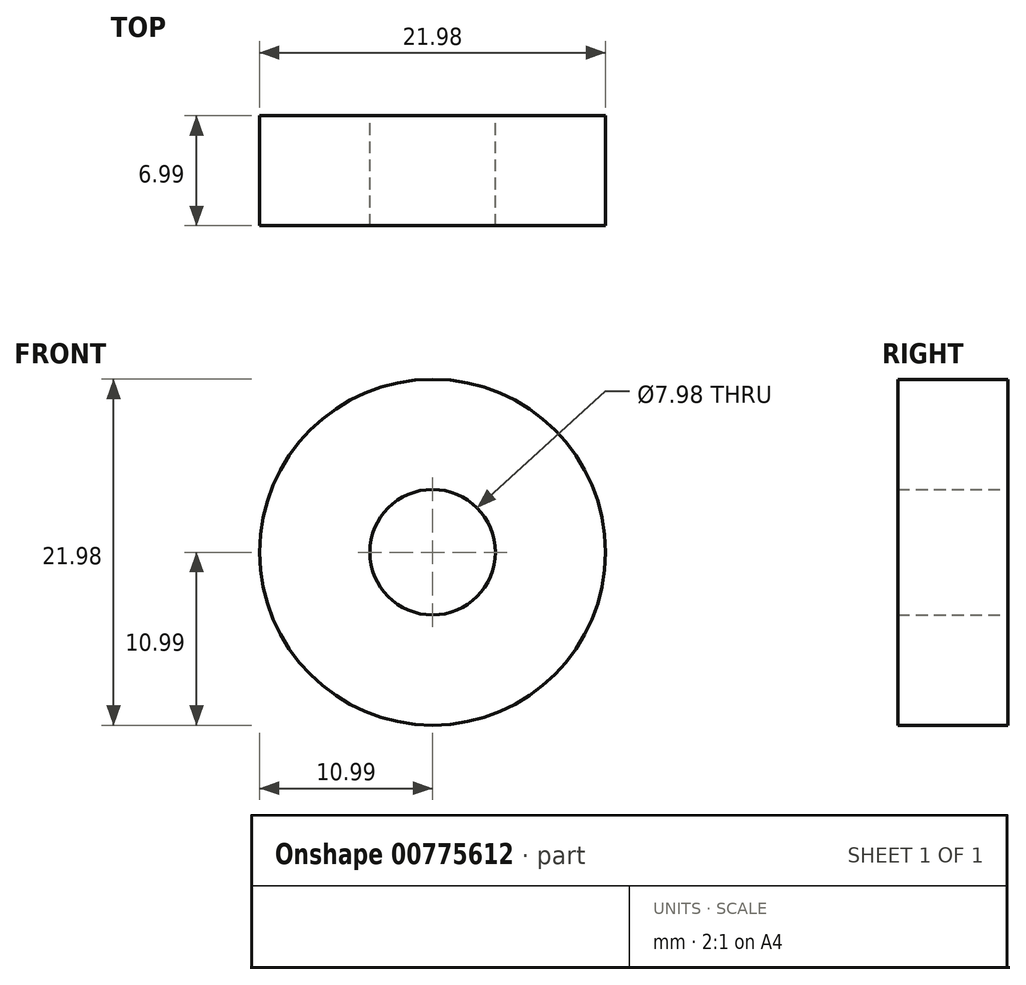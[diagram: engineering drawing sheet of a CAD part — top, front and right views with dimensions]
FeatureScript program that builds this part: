
annotation { "Feature Type Name" : "Feature", "Feature Type Description" : "" }
export const myFeature = defineFeature(function(context is Context, id is Id, definition is map)
    precondition{}
    {
        {
            var Q0;
            Q0=qCreatedBy(makeId("Front.planeOp"),FACE);
            var sketch = newSketch(context, id + "F0", { "sketchPlane" : qUnion([Q0])});
            skCircle(sketch, "E0", {"center": v(0, 0) * mm, "radius": 10.99 * mm});
            skCircle(sketch, "E1", {"center": v(0, 0) * mm, "radius": 3.99 * mm});
            skSolve(sketch);
        }
        {
            var Q0;
            Q0 = qSketchRegion(id + "F0", true);
            extrude(context, id + "F1", {"entities" : qUnion([Q0]), "depth" : 7 * mm, "offsetDistance" : 25.4 * mm});
        }
    });
